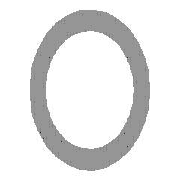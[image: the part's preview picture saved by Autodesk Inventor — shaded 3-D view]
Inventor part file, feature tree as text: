
AUTODESK INVENTOR PART (.ipt)
format: ipt  version: 2013 (Build 170138000, 138)  size: 109,056 bytes
history: native  units: mm (DEFAULTED — no unit token found)
features: other x4, sketch x3, plane x1
ambient origin geometry x8: Origin, YZ Plane, XZ Plane, XY Plane, X Axis, Y Axis, Z Axis, Center Point
bodies: Solid1 (feature_tree), Body (feature_tree)
feature tree (8):
  parser-record x1  (decoder bookkeeping rows leaked as tree rows — omitted from the tree; the rows remain in map.json)
  other  "Driven Length"
  other  "Start plane"
  other  "End plane"
  sketch  "Sketch"  dims[d2=355.6mm d3=0.0mm d4=-0.0mm d5=355.6mm d6=90.0deg d7=355.6mm]
  sketch  "Sketch3"  dims[d0=33.401mm]
  plane  "Work Plane3"
  sketch  "Sketch4"  dims[d1=3.3782mm]
